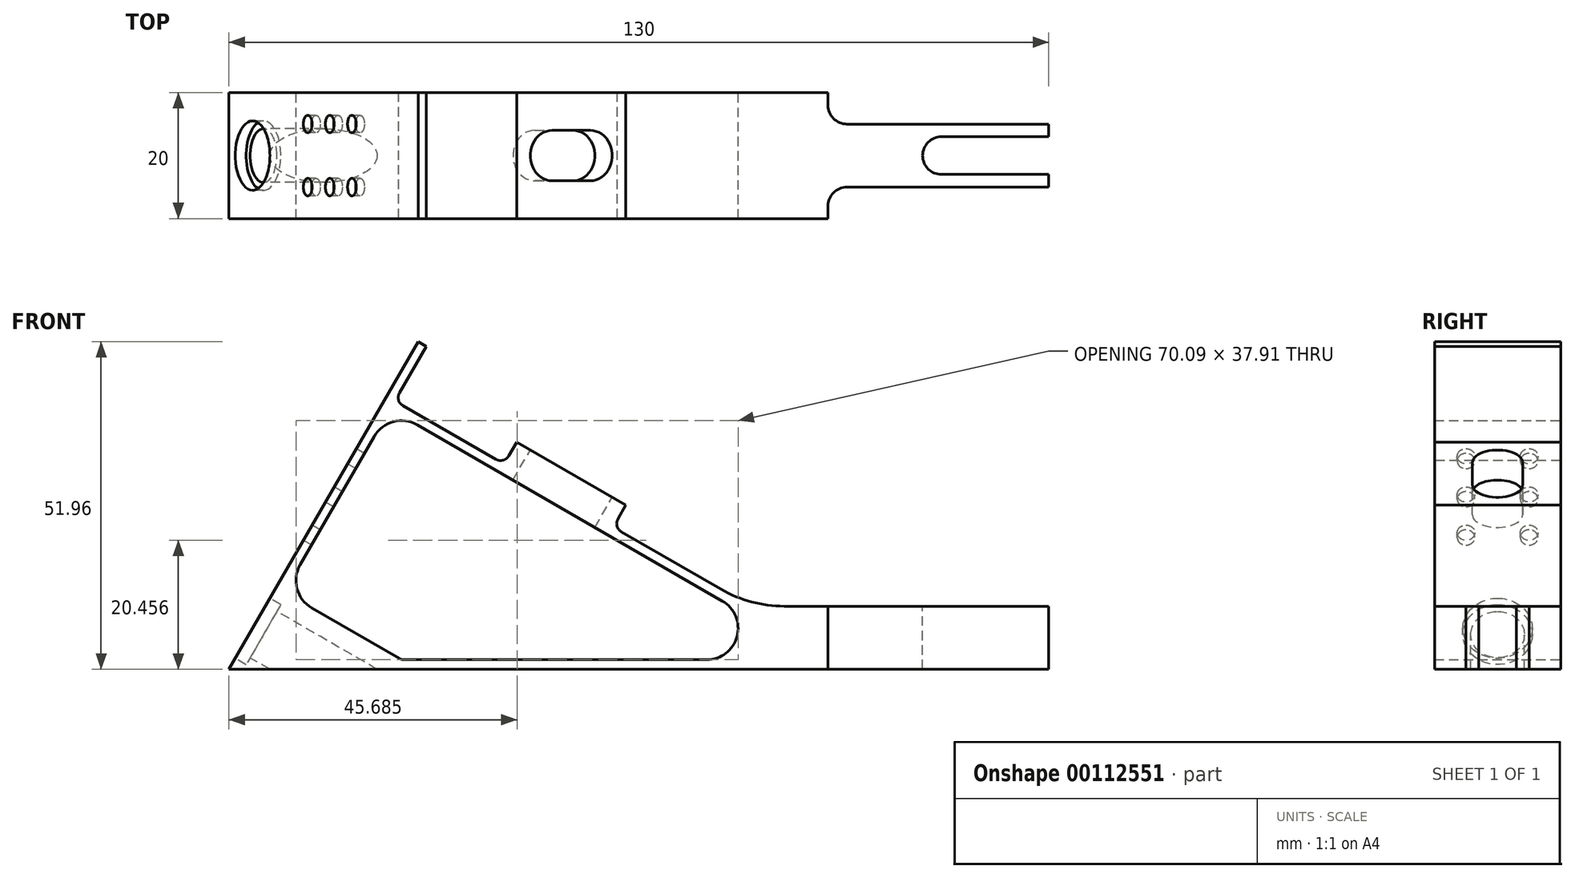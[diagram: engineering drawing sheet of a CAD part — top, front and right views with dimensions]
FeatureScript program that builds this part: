
annotation { "Feature Type Name" : "Feature", "Feature Type Description" : "" }
export const myFeature = defineFeature(function(context is Context, id is Id, definition is map)
    precondition{}
    {
        {
            var Q0;
            Q0=qCreatedBy(makeId("Front.planeOp"),FACE);
            var sketch = newSketch(context, id + "F0", { "sketchPlane" : qUnion([Q0])});
            skLineSegment(sketch, "E0", {"start": v(0, 0) * mm, "end": v(30, 51.96) * mm});
            skLineSegment(sketch, "E1", {"start": v(30, 51.96) * mm, "end": v(31.3, 51.21) * mm});
            skLineSegment(sketch, "E2", {"start": v(31.3, 51.21) * mm, "end": v(26.3, 42.55) * mm});
            skLineSegment(sketch, "E3", {"start": v(26.3, 42.55) * mm, "end": v(43.62, 32.55) * mm});
            skLineSegment(sketch, "E4", {"start": v(43.62, 32.55) * mm, "end": v(45.62, 36.02) * mm});
            skLineSegment(sketch, "E5", {"start": v(45.62, 36.02) * mm, "end": v(62.94, 26.02) * mm});
            skLineSegment(sketch, "E6", {"start": v(62.94, 26.02) * mm, "end": v(60.94, 22.55) * mm});
            skLineSegment(sketch, "E7", {"start": v(60.94, 22.55) * mm, "end": v(82.68, 10) * mm});
            skLineSegment(sketch, "E8", {"start": v(82.68, 10) * mm, "end": v(130, 10) * mm});
            skLineSegment(sketch, "E9", {"start": v(130, 10) * mm, "end": v(130, 0) * mm});
            skLineSegment(sketch, "E10", {"start": v(130, 0) * mm, "end": v(0, 0) * mm});
            skLineSegment(sketch, "E11", {"start": v(29.88, 38.75) * mm, "end": v(78.24, 10.83) * mm});
            skLineSegment(sketch, "E12", {"start": v(75.74, 1.5) * mm, "end": v(27.4, 1.5) * mm});
            skArc(sketch, "E13", {"start": v(75.74, 1.5) * mm, "mid": v(80.57, 5.2) * mm, "end": v(78.24, 10.83) * mm});
            skArc(sketch, "E14", {"start": v(29.88, 38.75) * mm, "mid": v(26.09, 39.25) * mm, "end": v(23.05, 36.92) * mm});
            skLineSegment(sketch, "E15", {"start": v(23.05, 36.92) * mm, "end": v(11.3, 16.57) * mm});
            skLineSegment(sketch, "E16", {"start": v(27.4, 1.5) * mm, "end": v(13.13, 9.74) * mm});
            skArc(sketch, "E17", {"start": v(11.3, 16.57) * mm, "mid": v(10.8, 12.78) * mm, "end": v(13.13, 9.74) * mm});
            skSolve(sketch);
        }
        {
            var Q0;
            Q0 = qSketchRegion(id + "F0", true);
            extrude(context, id + "F1", {"entities" : qUnion([Q0]), "depth" : 10 * mm, "hasSecondDirection" : true, "secondDirectionOppositeDirection" : true, "secondDirectionDepth" : 10 * mm});
        }
        {
            var Q0;
            Q0=makeQuery(id+"F1.opExtrude","SWEPT_FACE",FACE,{"disambiguationData":[OSD([sQuery(id+"F0.wireOp",EDGE,"E8")])]});
            var sketch = newSketch(context, id + "F2", { "sketchPlane" : qUnion([Q0])});
            skLineSegment(sketch, "E18", {"start": v(130, 5) * mm, "end": v(98, 5) * mm});
            skArc(sketch, "E19", {"start": v(95, 8) * mm, "mid": v(95.88, 5.88) * mm, "end": v(98, 5) * mm});
            skLineSegment(sketch, "E20", {"start": v(95, 8) * mm, "end": v(95, 10) * mm});
            skLineSegment(sketch, "E21", {"start": v(95, 10) * mm, "end": v(130, 10) * mm});
            skLineSegment(sketch, "E22", {"start": v(130, 10) * mm, "end": v(130, 5) * mm});
            skLineSegment(sketch, "E23", {"start": v(0, 0) * mm, "end": v(212.98, 0) * mm, "construction": true});
            skPoint(sketch, "E23.endSnap0", {"position": v(82.68, 0) * mm});
            skLineSegment(sketch, "E24", {"start": v(130, 3) * mm, "end": v(113, 3) * mm});
            skArc(sketch, "E25", {"start": v(113, 3) * mm, "mid": v(110.88, 2.12) * mm, "end": v(110, 0) * mm});
            skLineSegment(sketch, "E26", {"start": v(130, 3) * mm, "end": v(130, 0) * mm});
            skLineSegment(sketch, "E27.MirrorCS", {"start": v(95, -8) * mm, "end": v(95, -10) * mm});
            skLineSegment(sketch, "E28.MirrorCS", {"start": v(130, -5) * mm, "end": v(98, -5) * mm});
            skArc(sketch, "E29.MirrorCS", {"start": v(95, -8) * mm, "mid": v(95.88, -5.88) * mm, "end": v(98, -5) * mm});
            skLineSegment(sketch, "E30.MirrorCS", {"start": v(95, -10) * mm, "end": v(130, -10) * mm});
            skArc(sketch, "E31.MirrorCS", {"start": v(113, -3) * mm, "mid": v(110.88, -2.12) * mm, "end": v(110, 0) * mm});
            skLineSegment(sketch, "E32.MirrorCS", {"start": v(130, -10) * mm, "end": v(130, -5) * mm});
            skLineSegment(sketch, "E33.MirrorCS", {"start": v(130, -3) * mm, "end": v(130, 0) * mm});
            skLineSegment(sketch, "E34.MirrorCS", {"start": v(130, -3) * mm, "end": v(113, -3) * mm});
            skSolve(sketch);
        }
        {
            var Q0;
            Q0 = qSketchRegion(id + "F2", true);
            extrude(context, id + "F3", {"entities" : qUnion([Q0]), "operationType" : NewBodyOperationType.REMOVE, "endBound" : BoundingType.THROUGH_ALL, "oppositeDirection" : true, "depth" : 25 * mm});
        }
        {
            var Q0;
            Q0=makeQuery(id+"F1.opExtrude","SWEPT_FACE",FACE,{"disambiguationData":[OSD([sQuery(id+"F0.wireOp",EDGE,"E5")])]});
            var sketch = newSketch(context, id + "F4", { "sketchPlane" : qUnion([Q0])});
            skArc(sketch, "E35", {"start": v(35, -4) * mm, "mid": v(39, 0) * mm, "end": v(35, 4) * mm});
            skArc(sketch, "E36", {"start": v(28, 4) * mm, "mid": v(24, 0) * mm, "end": v(28, -4) * mm});
            skLineSegment(sketch, "E37", {"start": v(28, -4) * mm, "end": v(35, -4) * mm});
            skLineSegment(sketch, "E38", {"start": v(35, 4) * mm, "end": v(28, 4) * mm});
            skSolve(sketch);
        }
        {
            var Q0;
            Q0 = qSketchRegion(id + "F4", true);
            extrude(context, id + "F5", {"entities" : qUnion([Q0]), "operationType" : NewBodyOperationType.REMOVE, "endBound" : BoundingType.UP_TO_NEXT, "oppositeDirection" : true, "depth" : 25 * mm});
        }
        {
            var Q0;
            Q0=makeQuery(id+"F1.opExtrude","SWEPT_FACE",FACE,{"disambiguationData":[OSD([sQuery(id+"F0.wireOp",EDGE,"E0")])]});
            var sketch = newSketch(context, id + "F6", { "sketchPlane" : qUnion([Q0])});
            skCircle(sketch, "E39", {"center": v(-5, 39) * mm, "radius": 1.4 * mm});
            skCircle(sketch, "E40", {"center": v(5, 39) * mm, "radius": 1.4 * mm});
            skCircle(sketch, "E41", {"center": v(-5, 32) * mm, "radius": 1.4 * mm});
            skCircle(sketch, "E42", {"center": v(5, 32) * mm, "radius": 1.4 * mm});
            skCircle(sketch, "E43", {"center": v(-5, 25) * mm, "radius": 1.4 * mm});
            skCircle(sketch, "E44", {"center": v(5, 25) * mm, "radius": 1.4 * mm});
            skSolve(sketch);
        }
        {
            var Q0;
            Q0 = qSketchRegion(id + "F6", true);
            extrude(context, id + "F7", {"entities" : qUnion([Q0]), "operationType" : NewBodyOperationType.REMOVE, "endBound" : BoundingType.UP_TO_NEXT, "oppositeDirection" : true, "depth" : 25 * mm});
        }
        {
            var Q0;
            Q0=makeQuery(id+"F1.opExtrude","SWEPT_FACE",FACE,{"disambiguationData":[OSD([sQuery(id+"F0.wireOp",EDGE,"E0")])]});
            var sketch = newSketch(context, id + "F8", { "sketchPlane" : qUnion([Q0])});
            skCircle(sketch, "E45", {"center": v(0, 7.5) * mm, "radius": 5.5 * mm});
            skSolve(sketch);
        }
        {
            var Q0;
            Q0 = qSketchRegion(id + "F8", true);
            extrude(context, id + "F9", {"entities" : qUnion([Q0]), "operationType" : NewBodyOperationType.REMOVE, "oppositeDirection" : true, "depth" : 2 * mm});
        }
        {
            var Q0;
            Q0=makeQuery(id+"F9.boolean.opBoolean","COPY",FACE,{"derivedFrom":makeQuery(id+"F9.opExtrude","CAP_FACE",FACE,{"disambiguationData":[OSD([sQuery(id+"F8.wireOp",EDGE,"E45")])],"isStart":false})});
            var sketch = newSketch(context, id + "F10", { "sketchPlane" : qUnion([Q0])});
            skCircle(sketch, "E46", {"center": v(0, 7.5) * mm, "radius": 4.25 * mm});
            skSolve(sketch);
        }
        {
            var Q0;
            Q0 = qSketchRegion(id + "F10", true);
            extrude(context, id + "F11", {"entities" : qUnion([Q0]), "operationType" : NewBodyOperationType.REMOVE, "endBound" : BoundingType.THROUGH_ALL, "oppositeDirection" : true, "depth" : 25 * mm});
        }
        {
            var Q0;
            Q0=makeQuery(id+"F1.opExtrude","SWEPT_EDGE",EDGE,{"disambiguationData":[OSD([sQuery(id+"F0.wireOp",EDGE,"E2"),sQuery(id+"F0.wireOp",EDGE,"E3")])]});
            var Q1;
            Q1=makeQuery(id+"F1.opExtrude","SWEPT_EDGE",EDGE,{"disambiguationData":[OSD([sQuery(id+"F0.wireOp",EDGE,"E6"),sQuery(id+"F0.wireOp",EDGE,"E7")])]});
            var Q2;
            Q2=makeQuery(id+"F1.opExtrude","SWEPT_EDGE",EDGE,{"disambiguationData":[OSD([sQuery(id+"F0.wireOp",EDGE,"E12"),sQuery(id+"F0.wireOp",EDGE,"E16")])]});
            var Q3;
            Q3=makeQuery(id+"F1.opExtrude","SWEPT_EDGE",EDGE,{"disambiguationData":[OSD([sQuery(id+"F0.wireOp",EDGE,"E3"),sQuery(id+"F0.wireOp",EDGE,"E4")])]});
            fillet(context, id + "F12", {"entities" : qUnion([Q0, Q1, Q2, Q3]), "radius" : 1.5 * mm, "tangentPropagation" : true, "allowEdgeOverflow" : false});
        }
        {
            var Q0;
            Q0=makeQuery(id+"F1.opExtrude","SWEPT_EDGE",EDGE,{"disambiguationData":[OSD([sQuery(id+"F0.wireOp",EDGE,"E7"),sQuery(id+"F0.wireOp",EDGE,"E8")])]});
            fillet(context, id + "F13", {"entities" : qUnion([Q0]), "radius" : 20 * mm, "tangentPropagation" : true, "allowEdgeOverflow" : false});
        }
    });
